# Revit family: Alsanit - Kabiny sanitarne PERSEI - LPW
name_source: partatom
category: Doors
units: mm (PartAtom-declared; Revit-internal decimal feet)

## family parameters
Always vertical = Yes
Cut with Voids When Loaded = No
Room Calculation Point = No
Shared = No
Work Plane-Based = No

## types (2) — shared parameters
Analytic Construction = <None>
Autor = www.archispace.pl
Construction Type = Kabiny sanitarne
Define Thermal Properties by = Schematic Type
Description = Kabiny sanitarne to idealna kombinacja trwałości i estetyki w najnowszej cenie. Ze względu na estetyczność zastosowań jest najchętniej kupowanym systemem kabin sanitarnych w Polsce.
Film Instruktażowy = https://youtu.be
Function = Interior
Krótki opis = Kabiny sanitarne ALSANIT posiadające oznaczenie CE zgodnie z parametrami systemu
Lewa strona połączona typ = Rodzaj połączenia : Połączona
Lewa strona przy ścianie typ = Rodzaj połączenia : Przy ścianie
Lewa strona zamknięta typ = Rodzaj połączenia : Zamknięta
Manufacturer = Alsanit
Materiał belek = Alsanit - Aluminium
Materiał okuć = Alsanit - Aluminium
Materiał płyt = Alsanit - LPW - Biały 9016
Materiał wsporników = Alsanit - Aluminium
Model = PERSEI
Prawa strona połączona typ = Rodzaj połączenia : Połączona
Prawa strona przy ścianie typ = Rodzaj połączenia : Przy ścianie
Prawa strona zamknięta typ = Rodzaj połączenia : Zamknięta
Rodzaj płyt = LPW - Laminowana płyta wiórowa
Type Comments = Kabiny sanitarne (ścianki giszetowe do WC)
URL = https://www.alsanit.pl
Średnica nóżki 1 = 20 mm  [stored 0.0656168 ft]
Średnica nóżki 2 = 22 mm  [stored 0.0721785 ft]
Średnica nóżki 3 = 70 mm  [stored 0.229659 ft]
Średnica wspornika górnego = 57 mm  [stored 0.187008 ft]
zero-valued in all types: Default Elevation, Height, Rough Height, Rough Width, Width

## per-type parameters (varying)
| type | Grubość ścianki | Thickness |
| 18 mm | 18 mm  [stored 0.0590551 ft] | 18 mm  [stored 0.0590551 ft] |
| 28 mm | 28 mm  [stored 0.0918635 ft] | 28 mm  [stored 0.0918635 ft] |

note: [stored X ft] marks values corroborated as IEEE doubles in the binary element streams (Revit-internal decimal feet)

## geometry (parser evidence)
native form markers: Sweep x6
no freeform markers — native parametric forms only
